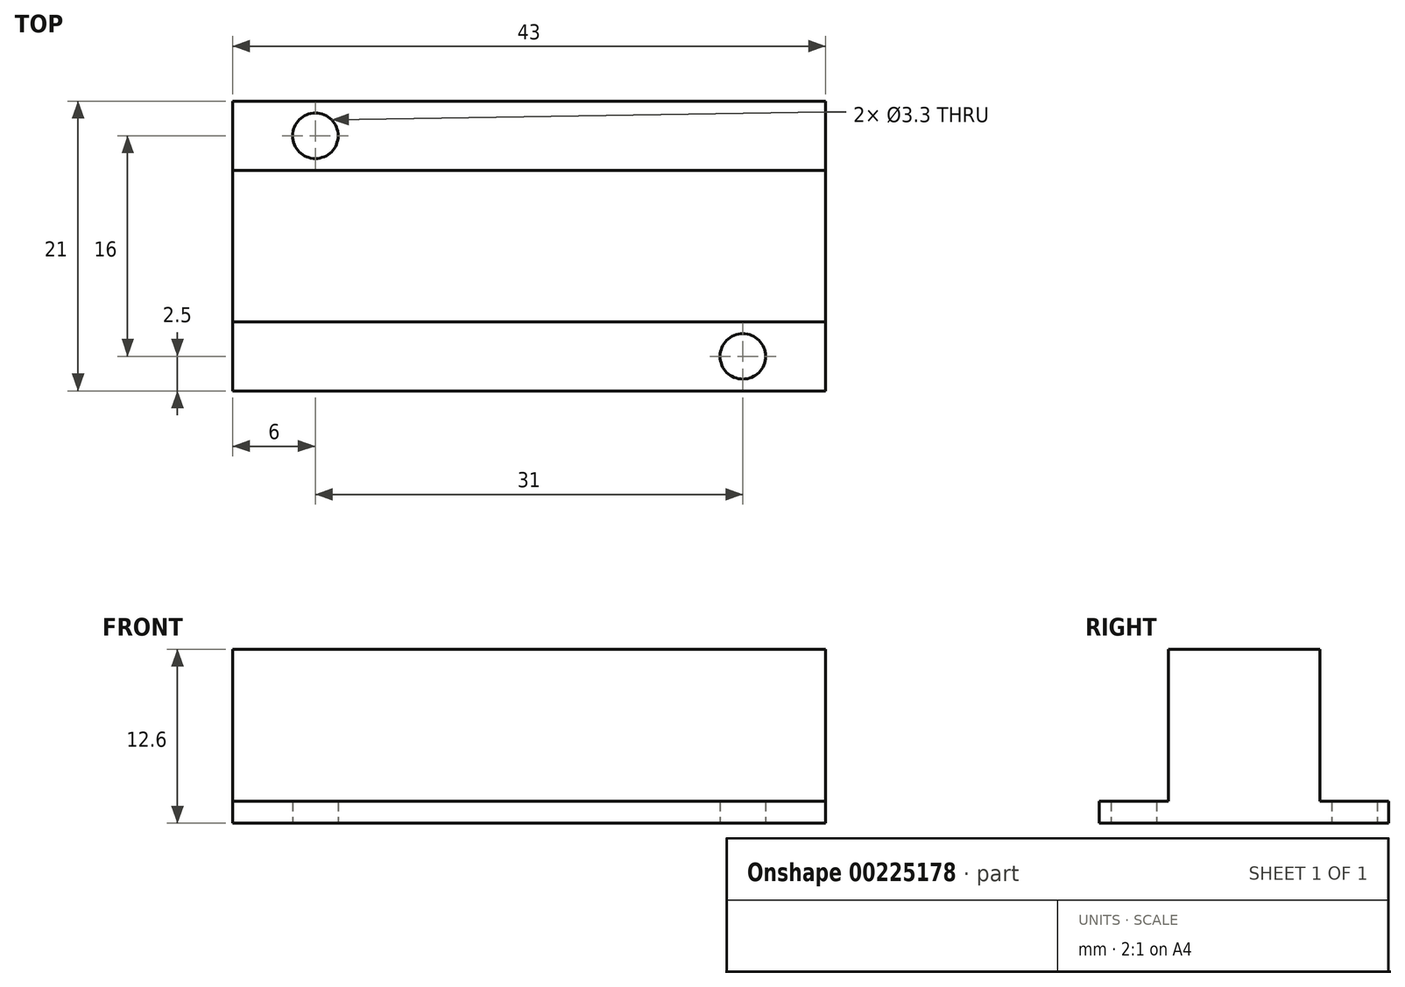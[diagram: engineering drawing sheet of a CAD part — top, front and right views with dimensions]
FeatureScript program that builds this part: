
annotation { "Feature Type Name" : "Feature", "Feature Type Description" : "" }
export const myFeature = defineFeature(function(context is Context, id is Id, definition is map)
    precondition{}
    {
        {
            var Q0;
            Q0=qCreatedBy(makeId("Top.planeOp"),FACE);
            var sketch = newSketch(context, id + "F0", { "sketchPlane" : qUnion([Q0])});
            skLineSegment(sketch, "E0.bottom", {"start": v(21.5, -10.5) * mm, "end": v(-21.5, -10.5) * mm});
            skLineSegment(sketch, "E0.top", {"start": v(21.5, 10.5) * mm, "end": v(-21.5, 10.5) * mm});
            skLineSegment(sketch, "E0.left", {"start": v(21.5, -10.5) * mm, "end": v(21.5, 10.5) * mm});
            skLineSegment(sketch, "E0.right", {"start": v(-21.5, -10.5) * mm, "end": v(-21.5, 10.5) * mm});
            skPoint(sketch, "E0.middle", {"position": v(0, 0) * mm});
            skCircle(sketch, "E1", {"center": v(-15.5, 8) * mm, "radius": 1.65 * mm});
            skCircle(sketch, "E2", {"center": v(15.5, -8) * mm, "radius": 1.65 * mm});
            skSolve(sketch);
        }
        {
            var Q0;
            {var subQ1=sQuery(id+"F0.wireOp",EDGE,"E0.top");Q0=makeQuery(id+"F0.imprint","IMPRINT",FACE,{"disambiguationData":[TD([[makeQuery(id+"F0.imprint","IMPRINT",EDGE,{"derivedFrom":subQ1}),1.0]])]});}
            var Q1;
            {var subQ1=sQuery(id+"F0.wireOp",EDGE,"E0.bottom");Q1=makeQuery(id+"F0.imprint","IMPRINT",FACE,{"disambiguationData":[TD([[makeQuery(id+"F0.imprint","IMPRINT",EDGE,{"derivedFrom":subQ1}),-1.0]])]});}
            extrude(context, id + "F1", {"entities" : qUnion([Q0, Q1]), "depth" : 1.6 * mm});
        }
        {
            var Q0;
            Q0=makeQuery(id+"F1.opExtrude","CAP_FACE",FACE,{"disambiguationData":[OSD([sQuery(id+"F0.wireOp",EDGE,"E0.bottom"),sQuery(id+"F0.wireOp",EDGE,"E0.top"),sQuery(id+"F0.wireOp",EDGE,"E0.left"),sQuery(id+"F0.wireOp",EDGE,"E0.right"),sQuery(id+"F0.wireOp",EDGE,"E1"),sQuery(id+"F0.wireOp",EDGE,"E2")])],"isStart":false});
            var sketch = newSketch(context, id + "F2", { "sketchPlane" : qUnion([Q0])});
            skLineSegment(sketch, "E3.bottom", {"start": v(21.5, -5.5) * mm, "end": v(-21.5, -5.5) * mm});
            skLineSegment(sketch, "E3.top", {"start": v(21.5, 5.5) * mm, "end": v(-21.5, 5.5) * mm});
            skLineSegment(sketch, "E3.left", {"start": v(21.5, -5.5) * mm, "end": v(21.5, 5.5) * mm});
            skPoint(sketch, "E3.middle", {"position": v(0, 0) * mm});
            skSolve(sketch);
        }
        {
            var Q0;
            Q0=qSketchRegion(id+"F2",true);
            var Q1;
            {var subQ0=sQuery(id+"F2.wireOp",EDGE,"E3.bottom");Q1=makeQuery(id+"F2.imprint","IMPRINT",FACE,{"disambiguationData":[TD([[makeQuery(id+"F2.imprint","IMPRINT",EDGE,{"derivedFrom":subQ0}),-1.0]])]});}
            extrude(context, id + "F3", {"entities" : qUnion([Q0, Q1]), "operationType" : NewBodyOperationType.ADD, "depth" : 11 * mm});
        }
    });
